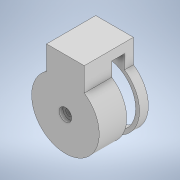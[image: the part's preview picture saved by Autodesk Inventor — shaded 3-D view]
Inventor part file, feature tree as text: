
AUTODESK INVENTOR PART (.ipt)
format: ipt  version: 2022 (Build 260153000, 153)  size: 172,544 bytes
history: native  units: mm
features: extrude x6, sketch x6
ambient origin geometry x8: Origin, YZ Plane, XZ Plane, XY Plane, X Axis, Y Axis, Z Axis, Center Point
bodies: Solid1 (feature_tree)
feature tree (12):
  extrude  "Extrusion1"  Depth=12.0mm TaperAngle=0.0deg
  extrude  "Extrusion2"  Depth=12.0mm TaperAngle=0.0deg
  extrude  "Extrusion3"  Depth=17.2mm TaperAngle=0.0deg
  extrude  "Extrusion4"  Depth=5.0mm TaperAngle=0.0deg
  extrude  "Extrusion5"  Depth=27.0mm TaperAngle=0.0deg
  extrude  "Extrusion6"  Depth=5.0mm TaperAngle=0.0deg
  sketch  "Sketch1"  dims[d1=5.0mm d5=12.0mm d6=0.0mm]
  sketch  "Sketch2"  dims[d9=20.0mm d10=12.0mm d11=0.0mm]
  sketch  "Sketch3"  dims[d12=13.0mm d13=17.2mm d14=0.0mm]
  sketch  "Sketch4"  dims[d15=17.0mm d16=5.0mm d17=0.0mm]
  sketch  "Sketch5"  dims[d18=9.0mm d19=27.0mm d20=0.0mm]
  sketch  "Sketch6"  dims[d21=17.0mm d22=5.0mm d23=0.0mm]
